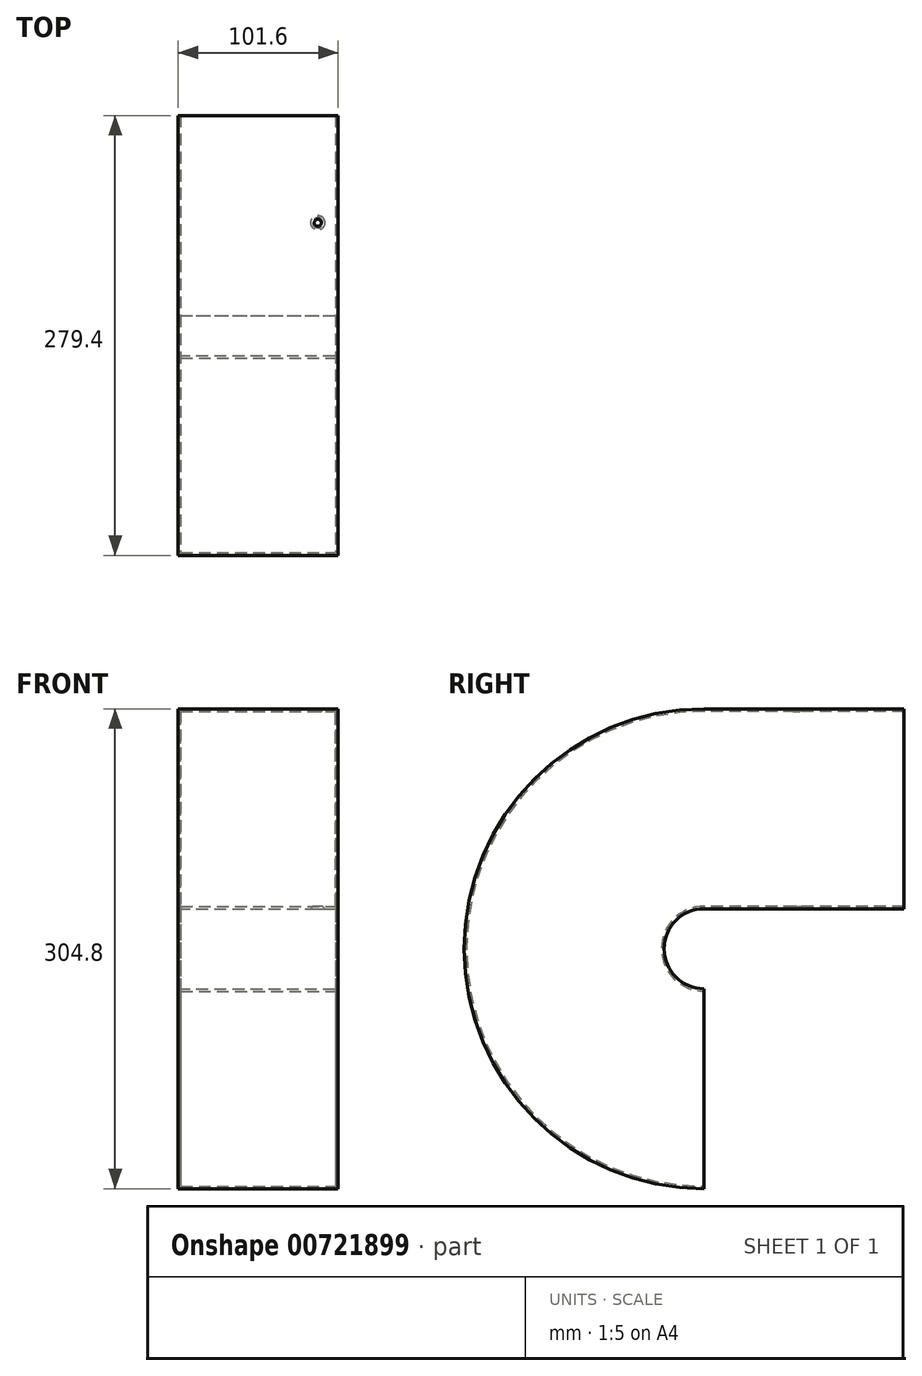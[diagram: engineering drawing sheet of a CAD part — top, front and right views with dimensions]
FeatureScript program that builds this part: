
annotation { "Feature Type Name" : "Feature", "Feature Type Description" : "" }
export const myFeature = defineFeature(function(context is Context, id is Id, definition is map)
    precondition{}
    {
        {
            var Q0;
            Q0=qCreatedBy(makeId("Front.planeOp"),FACE);
            var sketch = newSketch(context, id + "F0", { "sketchPlane" : qUnion([Q0])});
            skLineSegment(sketch, "E0.bottom", {"start": v(0, 0) * mm, "end": v(101.6, 0) * mm});
            skLineSegment(sketch, "E0.top", {"start": v(0, 127) * mm, "end": v(101.6, 127) * mm});
            skLineSegment(sketch, "E0.left", {"start": v(0, 0) * mm, "end": v(0, 127) * mm});
            skLineSegment(sketch, "E0.right", {"start": v(101.6, 0) * mm, "end": v(101.6, 127) * mm});
            skLineSegment(sketch, "E1.0", {"start": v(1.6, 125.4) * mm, "end": v(100, 125.4) * mm});
            skLineSegment(sketch, "E1.1", {"start": v(1.6, 1.6) * mm, "end": v(1.6, 125.4) * mm});
            skLineSegment(sketch, "E1.2", {"start": v(1.6, 1.6) * mm, "end": v(100, 1.6) * mm});
            skLineSegment(sketch, "E1.3", {"start": v(100, 1.6) * mm, "end": v(100, 125.4) * mm});
            skSolve(sketch);
        }
        {
            var Q0;
            Q0=qCreatedBy(makeId("Right.planeOp"),FACE);
            var sketch = newSketch(context, id + "F1", { "sketchPlane" : qUnion([Q0])});
            skLineSegment(sketch, "E2", {"start": v(-127, 0) * mm, "end": v(0, 0) * mm});
            skArc(sketch, "E3", {"start": v(-127, 0) * mm, "mid": v(-152.4, -25.4) * mm, "end": v(-127, -50.8) * mm});
            skSolve(sketch);
        }
        {
            var Q0;
            Q0 = qSketchRegion(id + "F0", true);
            var Q1;
            Q1 = qBodyType(qCreatedBy(id + "F1" ,EDGE), BodyType.WIRE);
            sweep(context, id + "F2", {"profiles" : qUnion([Q0]), "path" : qUnion([Q1])});
        }
        {
            var Q0;
            Q0=makeQuery(id+"F2.opSweep","SWEPT_FACE",FACE,{"disambiguationData":[OSD([sQuery(id+"F0.wireOp",EDGE,"E0.left"),sQuery(id+"F1.wireOp",EDGE,"E2")])]});
            var sketch = newSketch(context, id + "F3", { "sketchPlane" : qUnion([Q0])});
            skPoint(sketch, "E4", {"position": v(191.7, -93.32) * mm});
            skPoint(sketch, "E5", {"position": v(226.47, -26.7) * mm});
            skPoint(sketch, "E6", {"position": v(171.22, 50) * mm});
            skPoint(sketch, "E7", {"position": v(88.68, 68.2) * mm});
            skPoint(sketch, "E8.0.start.orphan", {"position": v(0, 63.5) * mm});
            skSolve(sketch);
        }
        {
            var Q0;
            Q0=sQuery(id+"F3.wireOp",VERTEX,"E4");
            var Q1;
            Q1=sQuery(id+"F3.wireOp",VERTEX,"E5");
            var Q2;
            Q2=sQuery(id+"F3.wireOp",VERTEX,"E6");
            var Q3;
            Q3=sQuery(id+"F3.wireOp",VERTEX,"E7");
            var Q4;
            Q4=makeQuery(id+"F2.opSweep","SWEPT_BODY",BODY,{"disambiguationData":[OSD([sQuery(id+"F0.wireOp",EDGE,"E0.bottom"),sQuery(id+"F0.wireOp",EDGE,"E0.top"),sQuery(id+"F0.wireOp",EDGE,"E0.left"),sQuery(id+"F0.wireOp",EDGE,"E0.right"),sQuery(id+"F0.wireOp",EDGE,"E1.0"),sQuery(id+"F0.wireOp",EDGE,"E1.1"),sQuery(id+"F0.wireOp",EDGE,"E1.2"),sQuery(id+"F0.wireOp",EDGE,"E1.3"),sQuery(id+"F1.wireOp",EDGE,"E3")])]});
            hole(context, id + "F4", {"style" : HoleStyle.C_SINK, "endStyle" : HoleEndStyle.THROUGH, "standardTappedOrClearance" : lookupTablePath({ "standard" : "ANSI", "fit" : "Normal (ASME)", "size" : "#8", "type" : "Clearance" }), "standardBlindInLast" : lookupTablePath({ "fit" : "Free", "standard" : "ANSI", "size" : "#8", "type" : "Clearance" }), "holeDiameter" : 4.5 * mm, "cSinkDiameter" : 9.12 * mm, "cSinkAngle" : 82 * degree, "majorDiameter" : 6.35 * mm, "isTappedThrough" : true, "tappedDepth" : 12.7 * mm, "tapClearance" : 3, "startFromSketch" : true, "locations" : qUnion([Q0, Q1, Q2, Q3]), "scope" : qUnion([Q4])});
        }
    });
